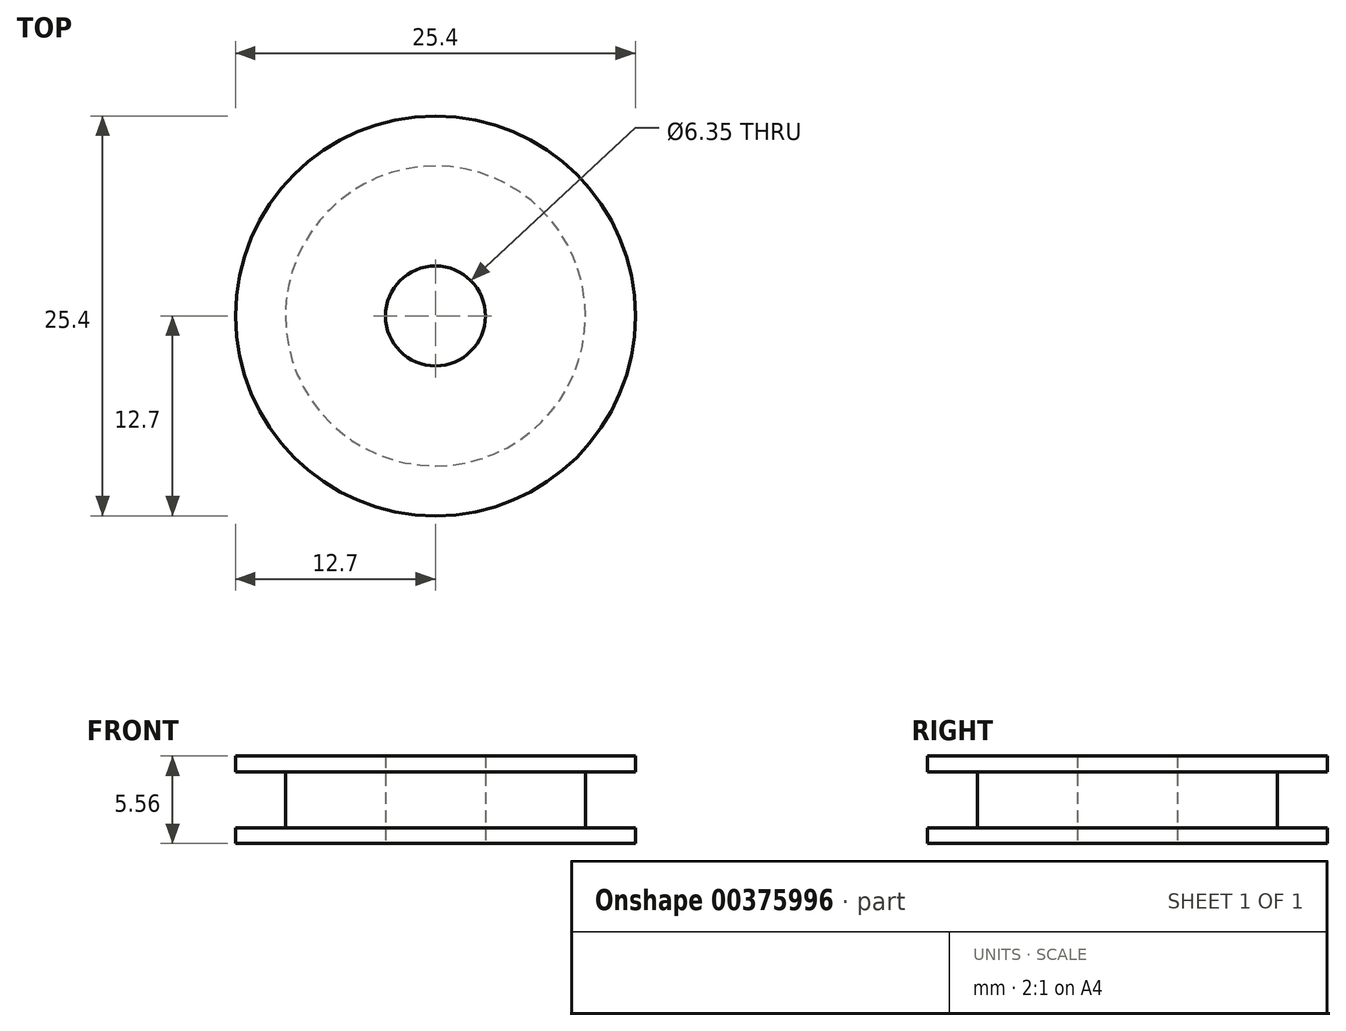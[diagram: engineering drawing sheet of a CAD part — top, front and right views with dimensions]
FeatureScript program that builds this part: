
annotation { "Feature Type Name" : "Feature", "Feature Type Description" : "" }
export const myFeature = defineFeature(function(context is Context, id is Id, definition is map)
    precondition{}
    {
        {
            var Q0;
            Q0=qCreatedBy(makeId("Top.planeOp"),FACE);
            var sketch = newSketch(context, id + "F0", { "sketchPlane" : qUnion([Q0])});
            skCircle(sketch, "E0", {"center": v(0, 0) * mm, "radius": 12.7 * mm});
            skCircle(sketch, "E1", {"center": v(0, 0) * mm, "radius": 3.18 * mm});
            skSolve(sketch);
        }
        {
            var Q0;
            Q0 = qSketchRegion(id + "F0", true);
            var Q1;
            Q1 = qSketchRegion(id + "F2", true);
            extrude(context, id + "F1", {"entities" : qUnion([Q0, Q1]), "depth" : 1 * mm});
        }
        {
            var Q0;
            Q0=makeQuery(id+"F1.opExtrude","CAP_FACE",FACE,{"disambiguationData":[OSD([sQuery(id+"F0.wireOp",EDGE,"E0"),sQuery(id+"F0.wireOp",EDGE,"E1")])],"isStart":false});
            var sketch = newSketch(context, id + "F2", { "sketchPlane" : qUnion([Q0])});
            skCircle(sketch, "E2", {"center": v(0, 0) * mm, "radius": 9.53 * mm});
            skSolve(sketch);
        }
        {
            var Q0;
            Q0=makeQuery(id+"F2.imprint","IMPRINT",FACE,{"disambiguationData":[TD([[makeQuery(id+"F2.imprint","IMPRINT",EDGE,{"derivedFrom":sQuery(id+"F2.wireOp",EDGE,"E2")}),1.0]])]});
            var Q1;
            Q1 = qSketchRegion(id + "F4", true);
            extrude(context, id + "F3", {"entities" : qUnion([Q0, Q1]), "operationType" : NewBodyOperationType.ADD, "depth" : 3.56 * mm});
        }
        {
            var Q0;
            Q0=makeQuery(id+"F3.opExtrude","CAP_FACE",FACE,{"disambiguationData":[OSD([sQuery(id+"F0.wireOp",EDGE,"E1"),sQuery(id+"F2.wireOp",EDGE,"E2")])],"isStart":false});
            var sketch = newSketch(context, id + "F4", { "sketchPlane" : qUnion([Q0])});
            skCircle(sketch, "E3", {"center": v(0, 0) * mm, "radius": 12.7 * mm});
            skSolve(sketch);
        }
        {
            var Q0;
            Q0=makeQuery(id+"F4.imprint","IMPRINT",FACE,{"disambiguationData":[TD([[makeQuery(id+"F4.imprint","IMPRINT",EDGE,{"derivedFrom":makeQuery(id+"F3.opExtrude","CAP_EDGE",EDGE,{"disambiguationData":[OSD([sQuery(id+"F2.wireOp",EDGE,"E2")])],"isStart":false})}),1.0]])]});
            var Q1;
            Q1=makeQuery(id+"F4.imprint","IMPRINT",FACE,{"disambiguationData":[TD([[makeQuery(id+"F4.imprint","IMPRINT",EDGE,{"derivedFrom":sQuery(id+"F4.wireOp",EDGE,"E3")}),1.0]])]});
            extrude(context, id + "F5", {"entities" : qUnion([Q0, Q1]), "operationType" : NewBodyOperationType.ADD, "depth" : 1 * mm});
        }
    });
